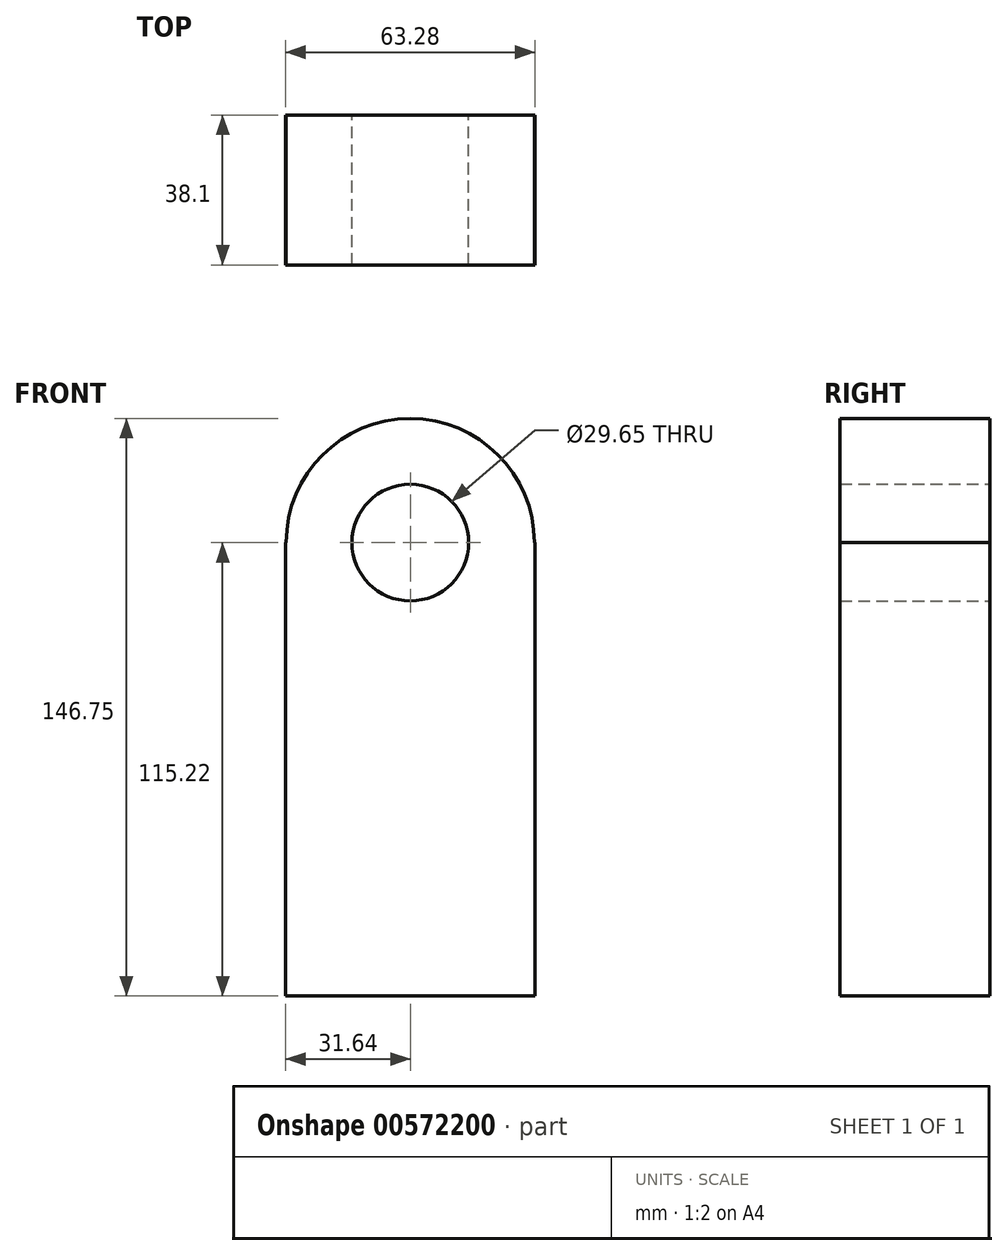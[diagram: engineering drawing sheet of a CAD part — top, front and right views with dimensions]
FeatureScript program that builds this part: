
annotation { "Feature Type Name" : "Feature", "Feature Type Description" : "" }
export const myFeature = defineFeature(function(context is Context, id is Id, definition is map)
    precondition{}
    {
        {
            var Q0;
            Q0=qCreatedBy(makeId("Front.planeOp"),FACE);
            var sketch = newSketch(context, id + "F0", { "sketchPlane" : qUnion([Q0])});
            skLineSegment(sketch, "E0.bottom", {"start": v(-31.64, 57.61) * mm, "end": v(-31.53, 57.61) * mm});
            skLineSegment(sketch, "E0.top", {"start": v(-31.64, -57.61) * mm, "end": v(31.64, -57.61) * mm});
            skLineSegment(sketch, "E0.left", {"start": v(-31.64, 57.61) * mm, "end": v(-31.64, -57.61) * mm});
            skLineSegment(sketch, "E0.right", {"start": v(31.64, 57.61) * mm, "end": v(31.64, -57.61) * mm});
            skPoint(sketch, "E0.middle", {"position": v(0, 0) * mm});
            skArc(sketch, "E1", {"start": v(31.53, 57.61) * mm, "mid": v(0, 89.14) * mm, "end": v(-31.53, 57.61) * mm});
            skCircle(sketch, "E2", {"center": v(0, 57.61) * mm, "radius": 14.83 * mm});
            skLineSegment(sketch, "E3.trimOffspring", {"start": v(31.53, 57.61) * mm, "end": v(31.64, 57.61) * mm});
            skSolve(sketch);
        }
        {
            var Q0;
            Q0=makeQuery(id+"F0.imprint","IMPRINT",FACE,{"disambiguationData":[TD([[makeQuery(id+"F0.imprint","IMPRINT",EDGE,{"derivedFrom":sQuery(id+"F0.wireOp",EDGE,"E0.bottom")}),-1.0]])]});
            extrude(context, id + "F1", {"entities" : qUnion([Q0]), "depth" : 38.1 * mm, "offsetDistance" : 25.4 * mm});
        }
    });
